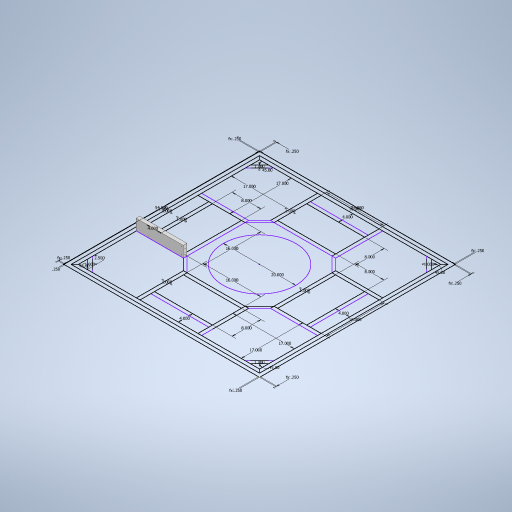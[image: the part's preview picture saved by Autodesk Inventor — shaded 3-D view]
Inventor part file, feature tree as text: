
AUTODESK INVENTOR PART (.ipt)
format: ipt  version: 2023 (Build 270158000, 158)  size: 370,688 bytes
history: native  units: in
note: dims shown in document units (in); Inventor stores cm internally (conversion verified against a paired STEP export)
features: extrude x5, sketch x5
ambient origin geometry x8: Origin, YZ Plane, XZ Plane, XY Plane, X Axis, Y Axis, Z Axis, Center Point
bodies: Solid1 (feature_tree)
feature tree (10):
  extrude  "Extrusion1"  Depth=54.0in
  extrude  "Extrusion2"  Depth=1.0in
  extrude  "Extrusion3"  Depth=16.0in
  extrude  "Extrusion4"  Depth=16.0in
  extrude  "Extrusion5"  Depth=3.0in
  sketch  "Sketch1"  dims[d0=54.0in d1=54.0in]
  sketch  "Sketch2"  dims[d2=1.0in d3=1.0in]
  sketch  "Sketch3"  dims[d4=8.0in d5=16.0in]
  sketch  "Sketch4"  dims[d6=8.0in d7=16.0in]
  sketch  "Sketch5"  dims[d8=16.0in d9=8.0in d10=16.0in d11=8.0in d12=4.0in d13=4.0in d14=4.0in d15=4.0in d16=17.0in d17=17.0in d18=17.0in d19=17.0in d20=20.0in d21=1.0in d22=1.0in d23=1.0in d24=1.0in d25=45.0deg d26=2.5in d27=45.0deg d28=45.0deg d29=45.0deg d30=1.0in d31=1.0in d32=1.0in d33=1.0in d34=0.25in d35=0.25in d36=0.25in d37=0.25in d38=0.25in d39=0.25in d40=0.25in d41=0.25in d42=3.0in d43=0.0in d44=0.125in d45=0.125in d46=0.5in d47=0.5in d48=0.5in d49=0.5in d50=1.0in d51=0.0in d52=0.125in d53=0.125in d54=0.5in d55=0.5in d56=0.5in d57=0.5in d58=2.0in d59=0.0in d60=0.125in d61=0.125in d62=0.5in d63=0.5in d64=1.0in d65=1.0in d66=1.0in d67=0.0in d68=0.125in d69=0.125in d70=0.5in d71=0.5in d72=0.5in d73=0.5in d74=3.0in d75=0.0in]
